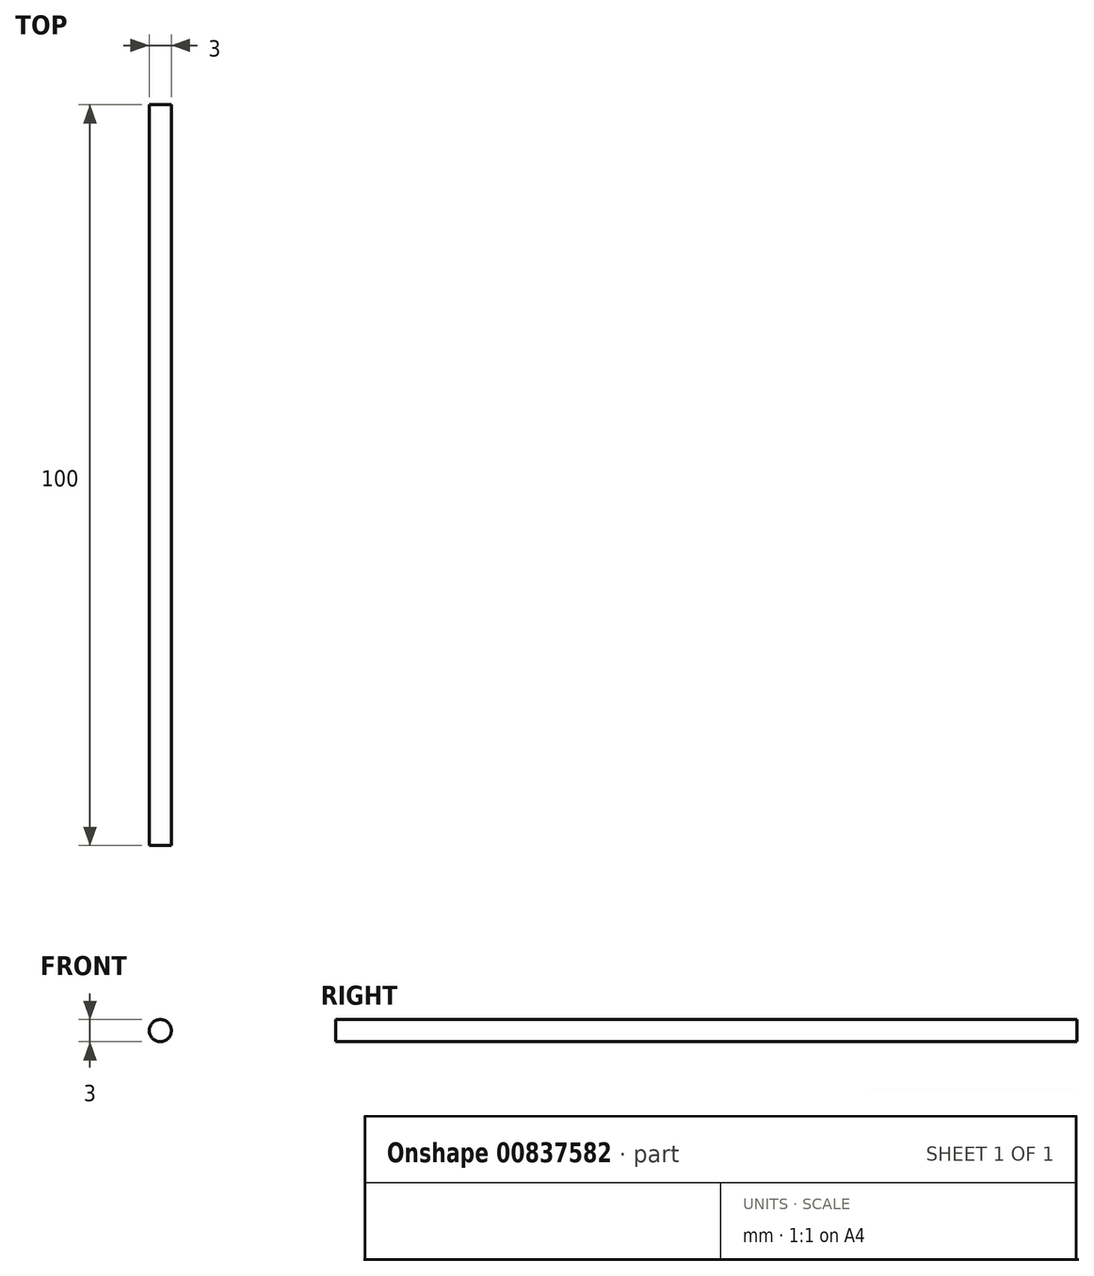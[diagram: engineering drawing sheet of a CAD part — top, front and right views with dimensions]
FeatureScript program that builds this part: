
annotation { "Feature Type Name" : "Feature", "Feature Type Description" : "" }
export const myFeature = defineFeature(function(context is Context, id is Id, definition is map)
    precondition{}
    {
        {
            var Q0;
            Q0=qCreatedBy(makeId("Front.planeOp"),FACE);
            var sketch = newSketch(context, id + "F0", { "sketchPlane" : qUnion([Q0])});
            skCircle(sketch, "E0", {"center": v(0, 0) * mm, "radius": 1.5 * mm});
            skSolve(sketch);
        }
        {
            var Q0;
            Q0 = qSketchRegion(id + "F0", true);
            extrude(context, id + "F1", {"entities" : qUnion([Q0]), "endBound" : BoundingType.SYMMETRIC, "depth" : 100 * mm, "offsetDistance" : 25 * mm});
        }
    });
